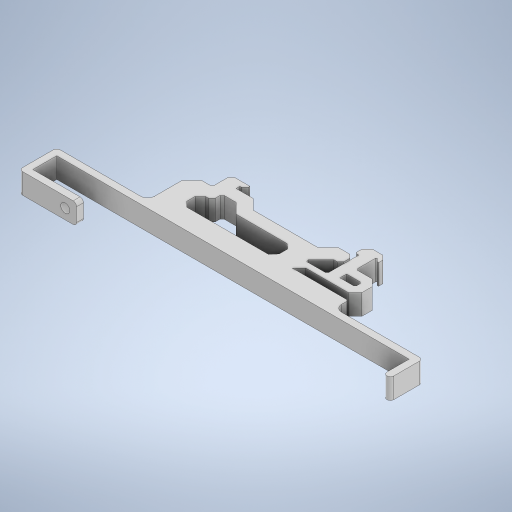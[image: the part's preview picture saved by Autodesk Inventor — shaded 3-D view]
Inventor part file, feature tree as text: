
AUTODESK INVENTOR PART (.ipt)
format: ipt  version: 2024 (Build 280153000, 153)  size: 458,240 bytes
history: native  units: in
note: dims shown in document units (in); Inventor stores cm internally (conversion verified against a paired STEP export)
features: extrude x3, sketch x3, fillet x2, projected_geometry x1
ambient origin geometry x8: Origin, YZ Plane, XZ Plane, XY Plane, X Axis, Y Axis, Z Axis, Center Point
bodies: Solid1 (feature_tree)
feature tree (9):
  extrude  "Extrusion1"  Depth=0.0394in
  fillet  "Fillet3"  Radius=4.2126in
  extrude  "Extrusion3"  Depth=1.0455in
  fillet  "Fillet4"  Radius=0.2362in
  extrude  "Extrusion4"  Depth=0.0787in
  sketch  "Sketch1"  dims[d8=0.2362in d9=0.0in]
  sketch  "Sketch3"  dims[d18=0.3758in d19=0.1566in d20=0.1762in d21=0.1957in d22=0.1387in d23=0.1174in d24=0.0391in d25=0.0157in d26=2.1217in d27=0.0973in d28=0.0587in d29=0.0587in d30=0.0548in d31=0.0235in d32=0.9395in d33=0.0587in d34=0.0973in d35=0.5854in d36=0.1174in d37=0.7438in d38=0.1174in d39=0.1174in d40=0.137in d41=0.1475in d42=0.0277in d43=0.2143in d44=0.3464in d45=0.0196in d46=0.0626in d47=0.0137in d48=0.0274in d49=0.0607in d50=0.1213in d51=0.047in d52=0.0509in d53=0.0157in d54=0.0356in d55=0.0094in d56=0.2063in d57=0.0196in d58=0.1664in d59=0.0783in d60=0.1174in d61=0.0783in d62=0.4893in d63=0.0783in d64=0.6302in d65=0.0156in d66=0.1253in d67=0.1174in d68=0.1174in d69=0.1174in d70=0.0391in d71=0.0391in d72=0.0391in d73=0.1475in d74=0.0695in d75=0.0391in d76=0.0391in d77=0.0196in d78=0.0196in d79=0.0196in d80=0.0196in d81=0.0196in d82=0.0658in d83=0.0235in d84=0.0587in d85=0.0391in d86=0.0391in d87=0.0391in d88=0.0626in d89=0.0548in d90=0.0156in d91=0.0471in d92=0.0607in d93=0.0137in d94=0.0196in d95=0.094in d96=0.0196in d97=0.0156in d98=0.1376in d99=0.0352in d100=0.2349in d101=0.1566in d102=0.3568in d103=0.1566in d104=0.0115in d105=0.0156in d106=0.0772in d107=0.1751in d108=0.0984in d109=0.118in]
  sketch  "Sketch4"  dims[d110=4.0551in d111=0.2756in d112=0.0787in d113=0.0787in d114=0.0787in d115=0.0787in d116=0.6614in d117=0.2953in d122=0.0394in d123=4.2126in d124=1.0455in d125=0.2362in d126=0.0in d127=0.0787in d128=0.1043in d129=0.2362in d130=0.4518in d131=0.1181in d133=0.3937in d134=0.0in]
  projected_geometry  "Projected Loop5"
